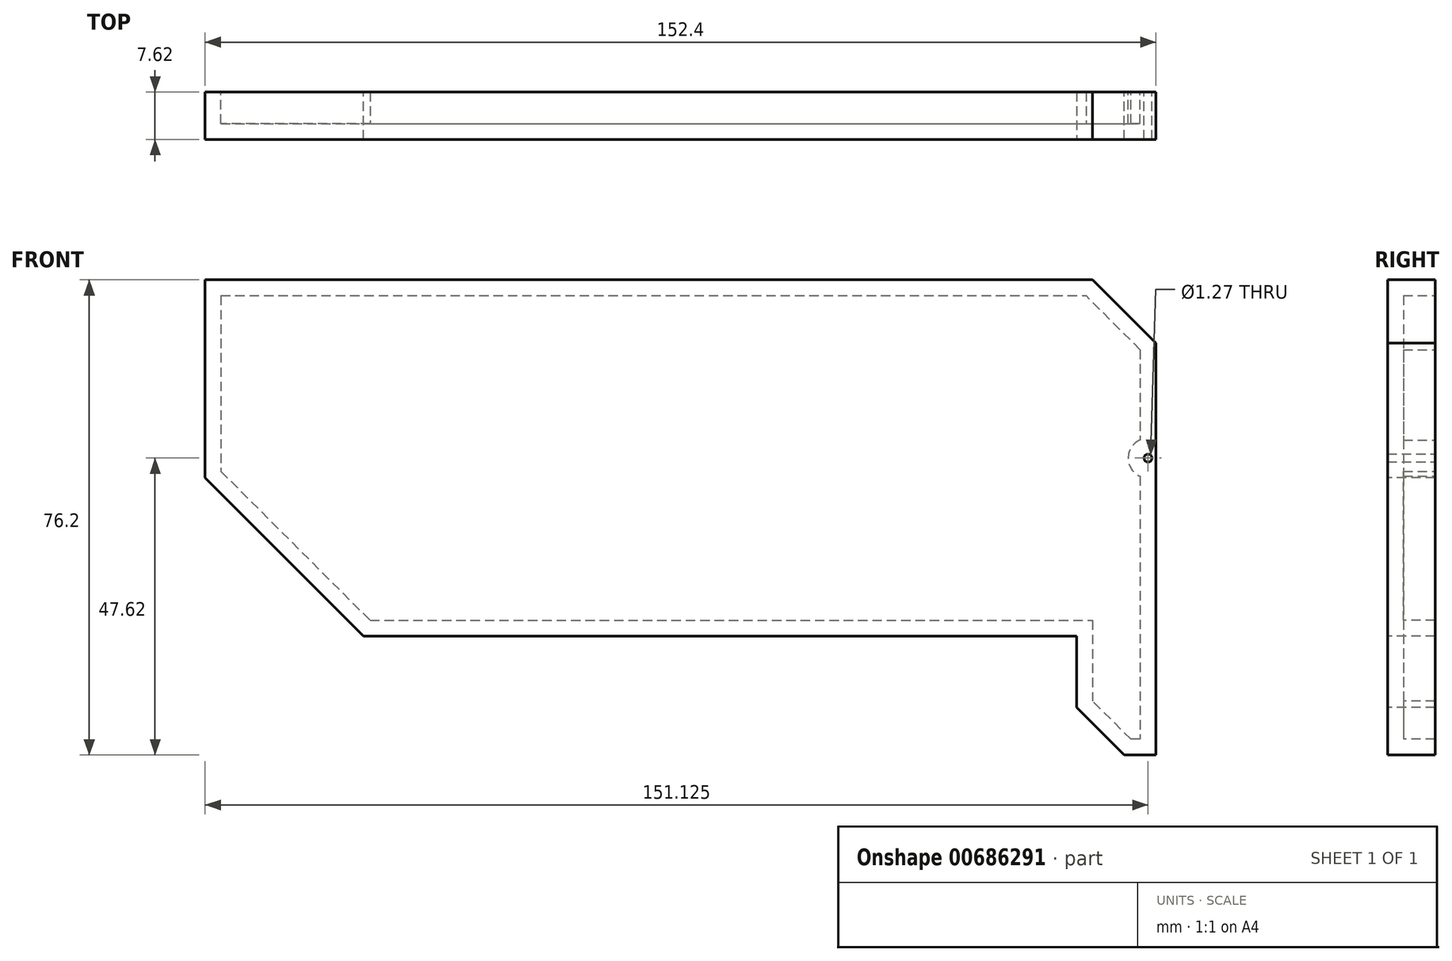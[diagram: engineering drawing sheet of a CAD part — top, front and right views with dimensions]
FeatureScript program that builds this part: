
annotation { "Feature Type Name" : "Feature", "Feature Type Description" : "" }
export const myFeature = defineFeature(function(context is Context, id is Id, definition is map)
    precondition{}
    {
        {
            var Q0;
            Q0=qCreatedBy(makeId("Front.planeOp"),FACE);
            var sketch = newSketch(context, id + "F0", { "sketchPlane" : qUnion([Q0])});
            skLineSegment(sketch, "E0.bottom", {"start": v(-76.2, 28.58) * mm, "end": v(76.2, 28.58) * mm});
            skLineSegment(sketch, "E0.top", {"start": v(-76.2, -28.57) * mm, "end": v(76.2, -28.57) * mm});
            skLineSegment(sketch, "E0.left", {"start": v(-76.2, 28.58) * mm, "end": v(-76.2, -28.57) * mm});
            skLineSegment(sketch, "E0.right", {"start": v(76.2, 28.58) * mm, "end": v(76.2, -28.57) * mm});
            skPoint(sketch, "E0.middle", {"position": v(0, 0) * mm});
            skCircle(sketch, "E1", {"center": v(74.93, 0) * mm, "radius": 0.64 * mm});
            skPoint(sketch, "E1.centerSnap0", {"position": v(76.2, 0) * mm});
            skSolve(sketch);
        }
        {
            var Q0;
            Q0=makeQuery(id+"F0.imprint","IMPRINT",FACE,{"disambiguationData":[TD([[makeQuery(id+"F0.imprint","IMPRINT",EDGE,{"derivedFrom":sQuery(id+"F0.wireOp",EDGE,"E0.bottom")}),-1.0]])]});
            extrude(context, id + "F1", {"entities" : qUnion([Q0]), "endBound" : BoundingType.SYMMETRIC, "depth" : 7.62 * mm, "offsetDistance" : 25.4 * mm});
        }
        {
            var Q0;
            Q0=makeQuery(id+"F1.opExtrude","SWEPT_EDGE",EDGE,{"disambiguationData":[OSD([sQuery(id+"F0.wireOp",EDGE,"E0.top"),sQuery(id+"F0.wireOp",EDGE,"E0.left")])]});
            chamfer(context, id + "F2", {"entities" : qUnion([Q0]), "width" : 25.4 * mm, "tangentPropagation" : true});
        }
        {
            var Q0;
            Q0=makeQuery(id+"F1.opExtrude","CAP_FACE",FACE,{"disambiguationData":[OSD([sQuery(id+"F0.wireOp",EDGE,"E0.bottom"),sQuery(id+"F0.wireOp",EDGE,"E0.top"),sQuery(id+"F0.wireOp",EDGE,"E0.left"),sQuery(id+"F0.wireOp",EDGE,"E0.right")])],"isStart":false});
            var sketch = newSketch(context, id + "F3", { "sketchPlane" : qUnion([Q0])});
            skLineSegment(sketch, "E2.bottom", {"start": v(76.2, -28.57) * mm, "end": v(63.5, -28.57) * mm});
            skLineSegment(sketch, "E2.top", {"start": v(76.2, -47.62) * mm, "end": v(63.5, -47.62) * mm});
            skLineSegment(sketch, "E2.left", {"start": v(76.2, -28.57) * mm, "end": v(76.2, -47.62) * mm});
            skLineSegment(sketch, "E2.right", {"start": v(63.5, -28.57) * mm, "end": v(63.5, -47.62) * mm});
            skSolve(sketch);
        }
        {
            var Q0;
            Q0=makeQuery(id+"F3.imprint","IMPRINT",FACE,{"disambiguationData":[TD([[makeQuery(id+"F3.imprint","IMPRINT",EDGE,{"derivedFrom":sQuery(id+"F3.wireOp",EDGE,"E2.bottom")}),-1.0]])]});
            extrude(context, id + "F4", {"entities" : qUnion([Q0]), "operationType" : NewBodyOperationType.ADD, "oppositeDirection" : true, "depth" : 7.62 * mm, "offsetDistance" : 25.4 * mm});
        }
        {
            var Q0;
            Q0=makeQuery(id+"F4.opExtrude","SWEPT_EDGE",EDGE,{"disambiguationData":[OSD([sQuery(id+"F3.wireOp",EDGE,"E2.top"),sQuery(id+"F3.wireOp",EDGE,"E2.right")])]});
            chamfer(context, id + "F5", {"entities" : qUnion([Q0]), "width" : 7.62 * mm, "tangentPropagation" : true});
        }
        {
            var Q0;
            Q0=makeQuery(id+"F1.opExtrude","SWEPT_EDGE",EDGE,{"disambiguationData":[OSD([sQuery(id+"F0.wireOp",EDGE,"E0.bottom"),sQuery(id+"F0.wireOp",EDGE,"E0.right")])]});
            chamfer(context, id + "F6", {"entities" : qUnion([Q0]), "width" : 10.16 * mm, "tangentPropagation" : true});
        }
        {
            var Q0;
            Q0=makeQuery(id+"F4.boolean.opBoolean","MERGE",FACE,{"derivedFrom":[makeQuery(id+"F1.opExtrude","CAP_FACE",FACE,{"disambiguationData":[OSD([sQuery(id+"F0.wireOp",EDGE,"E0.bottom"),sQuery(id+"F0.wireOp",EDGE,"E0.top"),sQuery(id+"F0.wireOp",EDGE,"E0.left"),sQuery(id+"F0.wireOp",EDGE,"E0.right")])],"isStart":true}),makeQuery(id+"F4.opExtrude","CAP_FACE",FACE,{"disambiguationData":[OSD([sQuery(id+"F3.wireOp",EDGE,"E2.bottom"),sQuery(id+"F3.wireOp",EDGE,"E2.top"),sQuery(id+"F3.wireOp",EDGE,"E2.left"),sQuery(id+"F3.wireOp",EDGE,"E2.right")])],"isStart":false})]});
            shell(context, id + "F7", {"entities" : qUnion([Q0]), "thickness" : 2.54 * mm});
        }
    });
